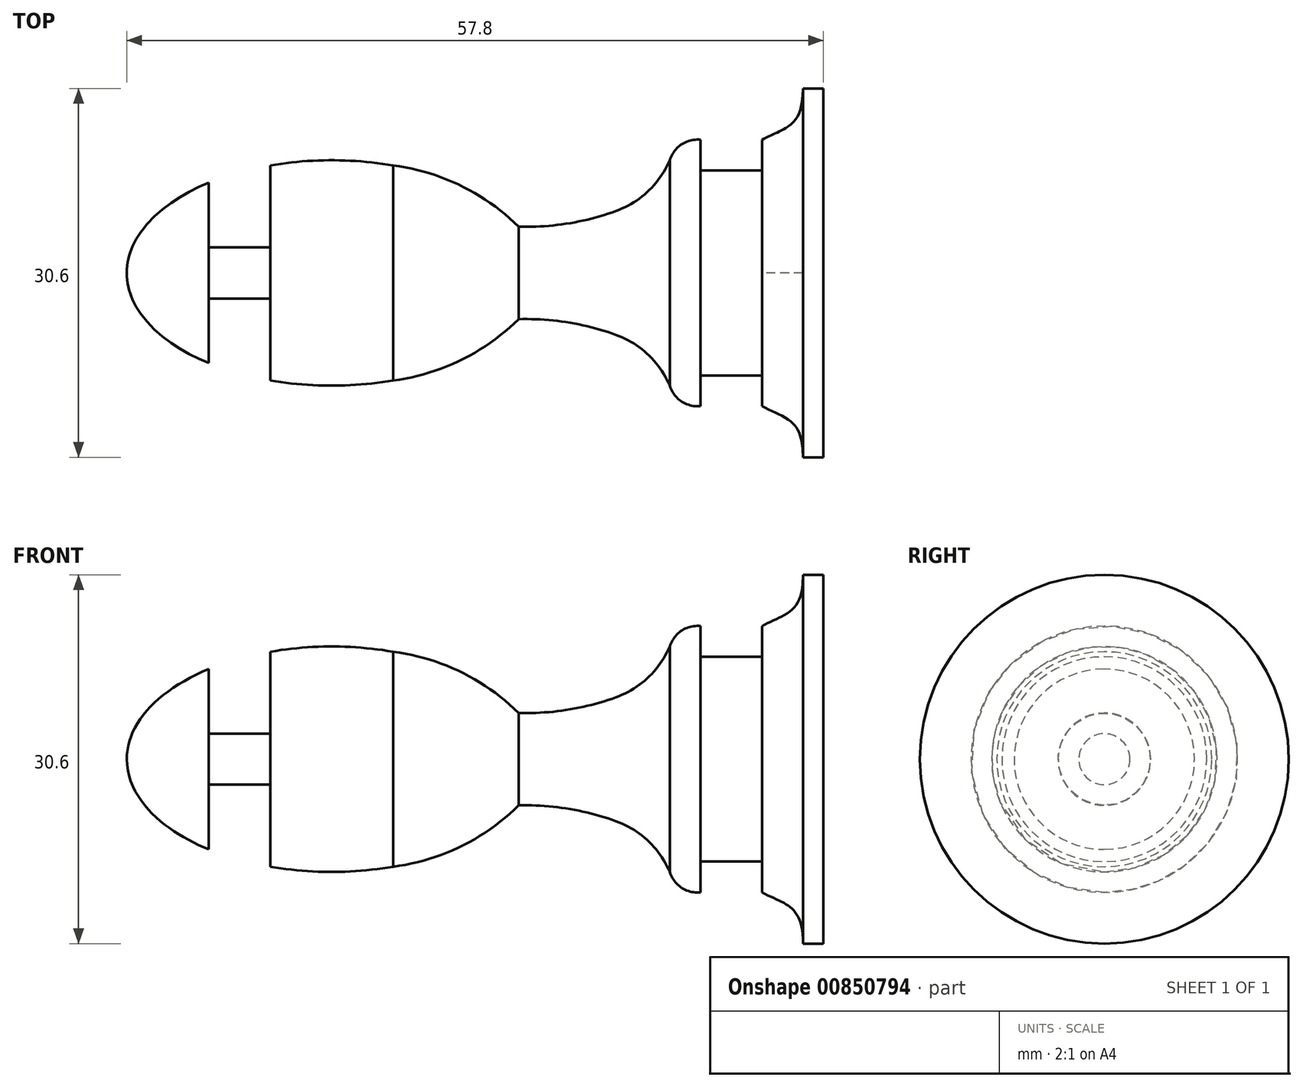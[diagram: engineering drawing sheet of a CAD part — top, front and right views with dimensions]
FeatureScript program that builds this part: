
annotation { "Feature Type Name" : "Feature", "Feature Type Description" : "" }
export const myFeature = defineFeature(function(context is Context, id is Id, definition is map)
    precondition{}
    {
        {
            var Q0;
            Q0=qCreatedBy(makeId("Front.planeOp"),FACE);
            var sketch = newSketch(context, id + "F0", { "sketchPlane" : qUnion([Q0])});
            skLineSegment(sketch, "E0", {"start": v(0, 0) * mm, "end": v(-34, 0) * mm});
            skLineSegment(sketch, "E1", {"start": v(0, 0) * mm, "end": v(0, 9) * mm});
            skPoint(sketch, "E2.orphan", {"position": v(-34, 9) * mm});
            skPoint(sketch, "E3.visualSharp", {"position": v(-34.34, -0.25) * mm});
            skLineSegment(sketch, "E4", {"start": v(-34, 0) * mm, "end": v(-34, 0) * mm});
            skLineSegment(sketch, "E5", {"start": v(-27, 1.25) * mm, "end": v(-30, 1.25) * mm});
            skLineSegment(sketch, "E6", {"start": v(-30, 1.25) * mm, "end": v(-30, 4.4) * mm});
            skLineSegment(sketch, "E7", {"start": v(-27, 1.25) * mm, "end": v(-27, 5.25) * mm});
            skEllipticalArc(sketch, "E8.trimOffspring", {});
            skPoint(sketch, "E9.start.orphan", {"position": v(-24.77, 1.25) * mm});
            skLineSegment(sketch, "E10", {"start": v(-24, 5.5) * mm, "end": v(-24, 0) * mm});
            skEllipticalArc(sketch, "E11", {});
            skPoint(sketch, "E12.MirrorCS.start.orphan", {"position": v(-21, 1.25) * mm});
            skPoint(sketch, "E13.MirrorCS.start.orphan", {"position": v(-18, 1.25) * mm});
            skPoint(sketch, "E14.orphan", {"position": v(-18, 4.4) * mm});
            skEllipticalArc(sketch, "E15.trimOffspring", {});
            skLineSegment(sketch, "E16", {"start": v(0, 9) * mm, "end": v(-1, 9) * mm});
            skLineSegment(sketch, "E17", {"start": v(-3, 6.5) * mm, "end": v(-3, 5) * mm});
            skLineSegment(sketch, "E18", {"start": v(-3, 5) * mm, "end": v(-6, 5) * mm});
            skLineSegment(sketch, "E19", {"start": v(-6, 5) * mm, "end": v(-6, 6.5) * mm});
            skFitSpline(sketch, "E20", {"points": [v(-1, 9) * mm, v(-3, 6.5) * mm], "startDerivative": vector(0, -5.74) * mm, "endDerivative": vector(-3.4, -1.84) * mm});
            skPoint(sketch, "E21", {"position": v(-1, 7.75) * mm});
            skPoint(sketch, "E22", {"position": v(-2, 6.5) * mm});
            skPoint(sketch, "E23", {"position": v(-6.75, 6.5) * mm});
            skLineSegment(sketch, "E24", {"start": v(-7.5, 5.5) * mm, "end": v(-7.5, 0) * mm});
            skLineSegment(sketch, "E25", {"start": v(-7.5, 0) * mm, "end": v(0, 0) * mm});
            skPoint(sketch, "E26.trimOffspring.end.orphan", {"position": v(-7.5, 6.5) * mm});
            skPoint(sketch, "E27.orphan", {"position": v(-1, 6.5) * mm});
            skLineSegment(sketch, "E28", {"start": v(0, 0) * mm, "end": v(0, 0) * mm});
            skArc(sketch, "E29", {"start": v(-6, 6.5) * mm, "mid": v(-6.93, 6.27) * mm, "end": v(-7.5, 5.5) * mm});
            skArc(sketch, "E30", {"start": v(-14.88, 2.26) * mm, "mid": v(-12.47, 2.42) * mm, "end": v(-10.12, 3.02) * mm});
            skArc(sketch, "E31", {"start": v(-10.12, 3.02) * mm, "mid": v(-8.56, 4) * mm, "end": v(-7.5, 5.5) * mm});
            skArc(sketch, "E32", {"start": v(-14.88, 2.26) * mm, "mid": v(-17.7, 4.26) * mm, "end": v(-21, 5.25) * mm});
            skPoint(sketch, "E33", {"position": v(-24, 5.5) * mm});
            skArc(sketch, "E34", {"start": v(-21, 5.25) * mm, "mid": v(-24, 5.5) * mm, "end": v(-27, 5.25) * mm});
            skPoint(sketch, "E35", {"position": v(-33.1, 2.28) * mm});
            const initialGuessF0  = {"E8.trimOffspring": [-0.02399875026965284, 0, -1, 0, 0.010001249730347161, 0.005500257719974544, 5.355796374407452, 0], "E11": [-0.024, 0, 0, 1, 0.0055, 0.01, 4.71238898038469, 5.1348990379194905], "E15.trimOffspring": [-0.024, 0, 0, 1, 0.0055, 0.01, 0.6433449016495061, 1.5707963267948966]};
            skSetInitialGuess(sketch, initialGuessF0);
            skSolve(sketch);
        }
        {
            var Q0;
            Q0=qSketchRegion(id+"F0",true);
            var Q1;
            Q1=sQuery(id+"F0.wireOp",EDGE,"E0");
            revolve(context, id + "F1", {"entities" : qUnion([Q0]), "axis" : qUnion([Q1]), "revolveType" : RevolveType.FULL});
        }
        {
            var Q0;
            Q0=makeQuery(id+"F1.opRevolve","SWEPT_BODY",BODY,{"disambiguationData":[OSD([sQuery(id+"F0.wireOp",EDGE,"E0"),sQuery(id+"F0.wireOp",EDGE,"E5"),sQuery(id+"F0.wireOp",EDGE,"E6"),sQuery(id+"F0.wireOp",EDGE,"E7"),sQuery(id+"F0.wireOp",EDGE,"E11"),sQuery(id+"F0.wireOp",EDGE,"E15.trimOffspring"),sQuery(id+"F0.wireOp",EDGE,"E1"),sQuery(id+"F0.wireOp",EDGE,"E16"),sQuery(id+"F0.wireOp",EDGE,"E17"),sQuery(id+"F0.wireOp",EDGE,"E18"),sQuery(id+"F0.wireOp",EDGE,"E19"),sQuery(id+"F0.wireOp",EDGE,"E20"),sQuery(id+"F0.wireOp",EDGE,"20765d3f-7415-4b65-9fd6-d6d3c09cccf2"),sQuery(id+"F0.wireOp",EDGE,"E25"),sQuery(id+"F0.wireOp",EDGE,"72a36f79-e602-4d31-8e08-93a80b1544a5")])]});
            var Q1;
            Q1=qCreatedBy(makeId("Origin.pointOp"),VERTEX);
            transform(context, id + "F2", {"entities" : qUnion([Q0]), "transformType" : TransformType.SCALE_UNIFORMLY, "scale" : 1.7, "scalePoint" : qUnion([Q1]), "makeCopy" : false});
        }
    });
